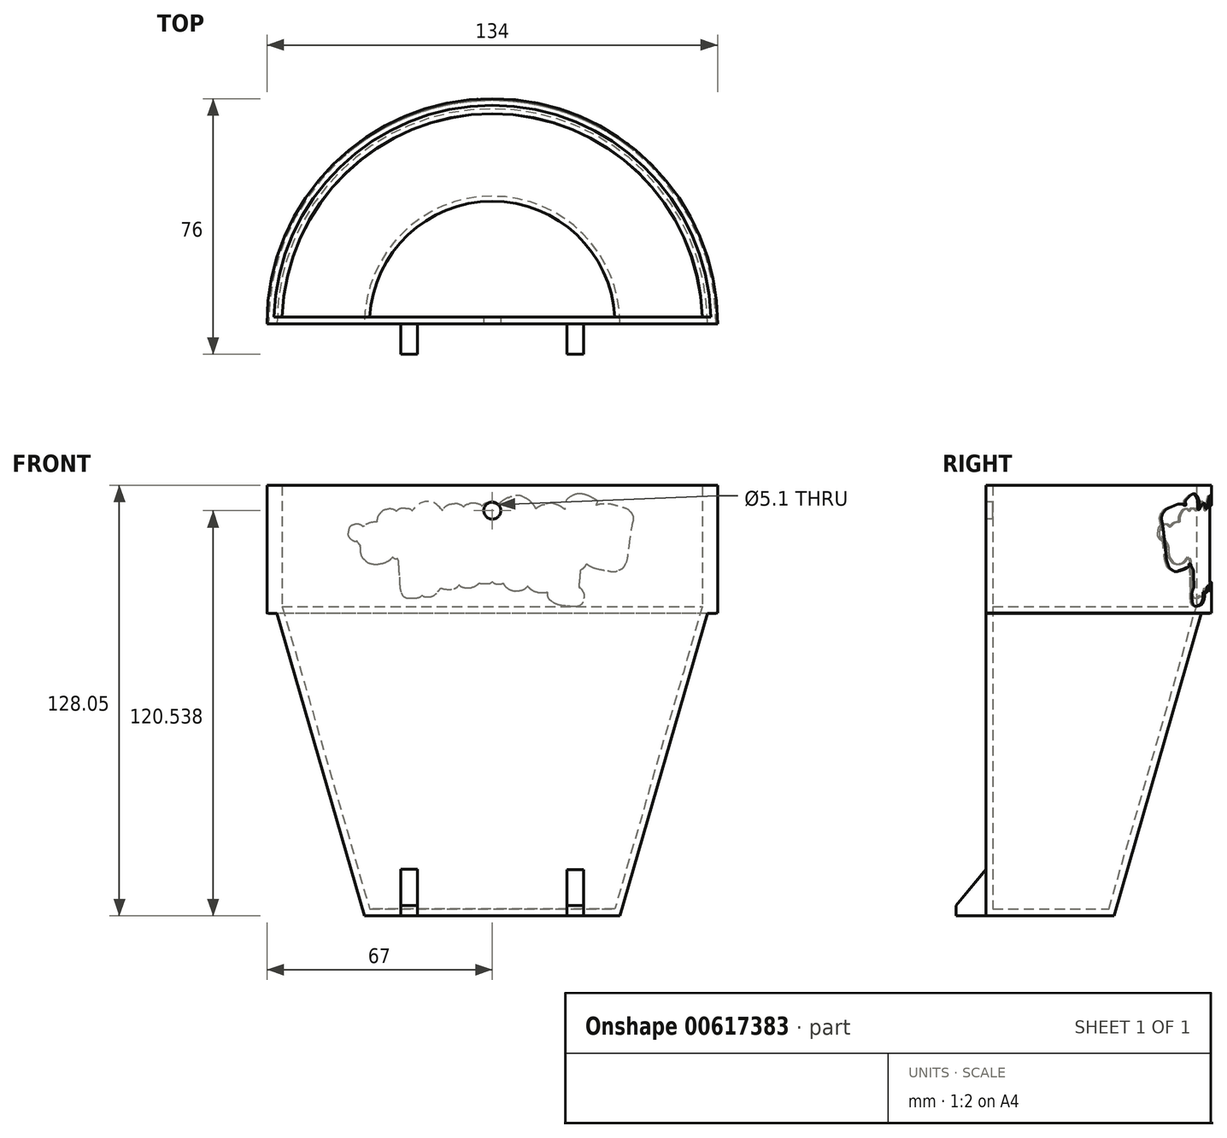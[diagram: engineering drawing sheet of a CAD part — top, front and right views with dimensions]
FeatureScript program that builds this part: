
annotation { "Feature Type Name" : "Feature", "Feature Type Description" : "" }
export const myFeature = defineFeature(function(context is Context, id is Id, definition is map)
    precondition{}
    {
        {
            var Q0;
            Q0=qCreatedBy(makeId("Front.planeOp"),FACE);
            var sketch = newSketch(context, id + "F0", { "sketchPlane" : qUnion([Q0])});
            skLineSegment(sketch, "E0", {"start": v(0, 56.42) * mm, "end": v(-67, 56.42) * mm});
            skLineSegment(sketch, "E1", {"start": v(-67, 56.42) * mm, "end": v(-67, 18.42) * mm});
            skLineSegment(sketch, "E2", {"start": v(0, -71.58) * mm, "end": v(-38, -71.58) * mm});
            skLineSegment(sketch, "E3", {"start": v(-67, 18.42) * mm, "end": v(-64, 18.42) * mm});
            skLineSegment(sketch, "E4", {"start": v(0, 56.42) * mm, "end": v(0, -71.58) * mm});
            skLineSegment(sketch, "E5", {"start": v(-64, 18.42) * mm, "end": v(-38, -71.58) * mm});
            skLineSegment(sketch, "E6.MirrorCS", {"start": v(0, 56.42) * mm, "end": v(67, 56.42) * mm});
            skLineSegment(sketch, "E7.MirrorCS", {"start": v(67, 56.42) * mm, "end": v(67, 18.42) * mm});
            skLineSegment(sketch, "E8.MirrorCS", {"start": v(67, 18.42) * mm, "end": v(64, 18.42) * mm});
            skLineSegment(sketch, "E9.MirrorCS", {"start": v(64, 18.42) * mm, "end": v(38, -71.58) * mm});
            skLineSegment(sketch, "E10.MirrorCS", {"start": v(0, -71.58) * mm, "end": v(38, -71.58) * mm});
            skSolve(sketch);
        }
        {
            var Q0;
            {var subQ0=sQuery(id+"F0.wireOp",EDGE,"E3");Q0=makeQuery(id+"F0.imprint","IMPRINT",FACE,{"disambiguationData":[TD([[makeQuery(id+"F0.imprint","IMPRINT",EDGE,{"derivedFrom":subQ0}),1.0]])]});}
            var Q1;
            {var subQ1=sQuery(id+"F0.wireOp",EDGE,"E0");Q1=makeQuery(id+"F0.imprint","IMPRINT",FACE,{"disambiguationData":[TD([[makeQuery(id+"F0.imprint","IMPRINT",EDGE,{"derivedFrom":subQ1}),1.0]])]});}
            var Q2;
            Q2=makeQuery(id+"F0.imprint","IMPRINT",FACE,{"disambiguationData":[TD([[makeQuery(id+"F0.imprint","IMPRINT",EDGE,{"derivedFrom":sQuery(id+"F0.wireOp",EDGE,"Kfnrekvc-ZjTY-c2iQ-cK4z-hKnBe4uEAVNk")}),1.0]])]});
            var Q3;
            Q3=sQuery(id+"F0.wireOp",EDGE,"E4");
            revolve(context, id + "F1", {"entities" : qUnion([Q0, Q1, Q2]), "axis" : qUnion([Q3]), "revolveType" : RevolveType.ONE_DIRECTION, "angle" : 180 * degree});
        }
        {
            var Q0;
            Q0=makeQuery(id+"FK2OT3XlAi37Aaq_1.splitOp","SPLIT",FACE,{"derivedFrom":makeQuery(id+"F1.opRevolve","SWEPT_FACE",FACE,{"disambiguationData":[OSD([sQuery(id+"F0.wireOp",EDGE,"E0")])]}),"isFromBackBody":true});
            shell(context, id + "F2", {"entities" : qUnion([Q0]), "thickness" : 2 * mm});
        }
        {
            var Q0;
            Q0=qCreatedBy(makeId("Front.planeOp"),FACE);
            var sketch = newSketch(context, id + "F3", { "sketchPlane" : qUnion([Q0])});
            skPoint(sketch, "E11.middle", {"position": v(0, -64.08) * mm});
            skLineSegment(sketch, "E12.bottom", {"start": v(-27.21, -56.57) * mm, "end": v(-22.21, -56.57) * mm});
            skLineSegment(sketch, "E12.top", {"start": v(-27.21, -71.57) * mm, "end": v(-22.21, -71.57) * mm});
            skLineSegment(sketch, "E12.left", {"start": v(-27.21, -56.57) * mm, "end": v(-27.21, -71.57) * mm});
            skLineSegment(sketch, "E12.right", {"start": v(-22.21, -56.57) * mm, "end": v(-22.21, -71.57) * mm});
            skPoint(sketch, "E12.middle", {"position": v(-24.71, -64.07) * mm});
            skLineSegment(sketch, "E13.bottom", {"start": v(22.21, -56.63) * mm, "end": v(27.21, -56.63) * mm});
            skLineSegment(sketch, "E13.top", {"start": v(22.21, -71.63) * mm, "end": v(27.21, -71.63) * mm});
            skLineSegment(sketch, "E13.left", {"start": v(22.21, -56.63) * mm, "end": v(22.21, -71.63) * mm});
            skLineSegment(sketch, "E13.right", {"start": v(27.21, -56.63) * mm, "end": v(27.21, -71.63) * mm});
            skPoint(sketch, "E13.middle", {"position": v(24.71, -64.13) * mm});
            skLineSegment(sketch, "E14", {"start": v(0, -71.68) * mm, "end": v(-22.21, -71.57) * mm, "construction": true});
            skLineSegment(sketch, "E15", {"start": v(0, -71.68) * mm, "end": v(22.21, -71.63) * mm, "construction": true});
            skSolve(sketch);
        }
        {
            var Q0;
            Q0=qSketchRegion(id+"F3",true);
            extrude(context, id + "F4", {"entities" : qUnion([Q0]), "operationType" : NewBodyOperationType.ADD, "depth" : 9 * mm});
        }
        {
            var Q0;
            Q0=qCreatedBy(makeId("Front.planeOp"),FACE);
            var sketch = newSketch(context, id + "F5", { "sketchPlane" : qUnion([Q0])});
            skCircle(sketch, "E16", {"center": v(0, 48.9) * mm, "radius": 2.55 * mm});
            skLineSegment(sketch, "E17", {"start": v(0, 56.46) * mm, "end": v(0, 51.46) * mm, "construction": true});
            skSolve(sketch);
        }
        {
            var Q0;
            {var subQ0=sQuery(id+"F5.wireOp",EDGE,"E16");var subQ1=sQuery(id+"F5.wireOp",EDGE,"mXHq6PA0-CqQh-Lv1D-GdnR-uttjTBgCqYAd");var subQ2=makeQuery(id+"F5.imprint","INTERSECT",VERTEX,{"disambiguationData":[OD(0.0)],"derivedFrom":[subQ1,subQ0]});Q0=makeQuery(id+"F5.imprint","IMPRINT",FACE,{"disambiguationData":[TD([[makeQuery(id+"F5.imprint","IMPRINT",EDGE,{"disambiguationData":[TD([[subQ2,1.0]])],"derivedFrom":subQ1}),1.0]])]});}
            var Q1;
            {var subQ0=sQuery(id+"F5.wireOp",EDGE,"E16");var subQ1=sQuery(id+"F5.wireOp",EDGE,"mXHq6PA0-CqQh-Lv1D-GdnR-uttjTBgCqYAd");var subQ2=makeQuery(id+"F5.imprint","INTERSECT",VERTEX,{"disambiguationData":[OD(0.0)],"derivedFrom":[subQ1,subQ0]});Q1=makeQuery(id+"F5.imprint","IMPRINT",FACE,{"disambiguationData":[TD([[makeQuery(id+"F5.imprint","IMPRINT",EDGE,{"disambiguationData":[TD([[subQ2,-1.0]])],"derivedFrom":subQ1}),-1.0]])]});}
            var Q2;
            {var subQ0=sQuery(id+"F5.wireOp",EDGE,"E16");var subQ1=sQuery(id+"F5.wireOp",EDGE,"mXHq6PA0-CqQh-Lv1D-GdnR-uttjTBgCqYAd");var subQ2=makeQuery(id+"F5.imprint","INTERSECT",VERTEX,{"disambiguationData":[OD(0.0)],"derivedFrom":[subQ1,subQ0]});Q2=makeQuery(id+"F5.imprint","IMPRINT",FACE,{"disambiguationData":[TD([[makeQuery(id+"F5.imprint","IMPRINT",EDGE,{"disambiguationData":[TD([[subQ2,-1.0]])],"derivedFrom":subQ1}),1.0]])]});}
            var Q3;
            Q3=makeQuery(id+"F5.imprint","IMPRINT",FACE,{"disambiguationData":[TD([[makeQuery(id+"F5.imprint","IMPRINT",EDGE,{"derivedFrom":sQuery(id+"F5.wireOp",EDGE,"3L3EtL6l-Z5xn-OpCV-56nK-jdjtkjkFmQCH")}),1.0]])]});
            var Q4;
            {var subQ0=sQuery(id+"F5.wireOp",EDGE,"E16");var subQ1=makeQuery(id+"F5.imprint","INTERSECT",VERTEX,{"derivedFrom":[subQ0,sQuery(id+"F5.wireOp",EDGE,"FsL0R7OM-7ciT-IbGp-vdo3-nhAMjBVExGBG")]});Q4=makeQuery(id+"F5.imprint","IMPRINT",FACE,{"disambiguationData":[TD([[makeQuery(id+"F5.imprint","IMPRINT",EDGE,{"disambiguationData":[TD([[subQ1,1.0]])],"derivedFrom":subQ0}),1.0]])]});}
            var Q5;
            Q5=sQuery(id+"F5.wireOp",EDGE,"mXHq6PA0-CqQh-Lv1D-GdnR-uttjTBgCqYAd");
            var Q6;
            Q6=sQuery(id+"F5.wireOp",EDGE,"E16");
            extrude(context, id + "F6", {"entities" : qUnion([Q0, Q1, Q2, Q3, Q4]), "operationType" : NewBodyOperationType.REMOVE, "surfaceEntities" : qUnion([Q5, Q6]), "oppositeDirection" : true, "depth" : 10 * mm, "offsetDistance" : 25 * mm});
        }
        {
            var Q0;
            Q0=makeQuery(id+"F4.opExtrude","CAP_EDGE",EDGE,{"disambiguationData":[OSD([sQuery(id+"F3.wireOp",EDGE,"E11.bottom")])],"isStart":false});
            var Q1;
            Q1=makeQuery(id+"F4.opExtrude","CAP_EDGE",EDGE,{"disambiguationData":[OSD([sQuery(id+"F3.wireOp",EDGE,"E12.bottom")])],"isStart":false});
            var Q2;
            Q2=makeQuery(id+"F4.opExtrude","CAP_EDGE",EDGE,{"disambiguationData":[OSD([sQuery(id+"F3.wireOp",EDGE,"E13.bottom")])],"isStart":false});
            chamfer(context, id + "F7", {"entities" : qUnion([Q0, Q1, Q2]), "chamferType" : ChamferType.OFFSET_ANGLE, "width" : 10 * mm, "oppositeDirection" : false, "angle" : 50 * degree, "tangentPropagation" : true});
        }
        {
            var Q0;
            Q0=makeQuery(id+"F2.opShell","OFFSET_FACE",FACE,{"disambiguationData":[OSD([sQuery(id+"F0.wireOp",EDGE,"E0"),sQuery(id+"F0.wireOp",EDGE,"E1"),sQuery(id+"F0.wireOp",EDGE,"E2"),sQuery(id+"F0.wireOp",EDGE,"E3"),sQuery(id+"F0.wireOp",EDGE,"E4"),sQuery(id+"F0.wireOp",EDGE,"E5")])]});
            cPlane(context, id + "F8", {"entities" : qUnion([Q0]), "cplaneType" : CPlaneType.OFFSET, "offset" : 66.8 * mm, "width" : 150 * mm, "height" : 150 * mm});
        }
        {
            var Q0;
            Q0=makeQuery(id+"F1.opRevolve","SWEPT_FACE",FACE,{"disambiguationData":[OSD([sQuery(id+"F0.wireOp",EDGE,"E0")])]});
            var sketch = newSketch(context, id + "F9", { "sketchPlane" : qUnion([Q0])});
            skCircle(sketch, "E18", {"center": v(0, 0) * mm, "radius": 67.75 * mm});
            skCircle(sketch, "E19", {"center": v(0, 0) * mm, "radius": 91 * mm});
            skSolve(sketch);
        }
        {
            var Q0;
            Q0=qSketchRegion(id+"F9",true);
            extrude(context, id + "F10", {"entities" : qUnion([Q0]), "operationType" : NewBodyOperationType.REMOVE, "oppositeDirection" : true, "depth" : 124 * mm});
        }
        {
            var Q0;
            Q0=qCreatedBy(id+"F8.planeOp",FACE);
            var sketch = newSketch(context, id + "F11", { "sketchPlane" : qUnion([Q0])});
            skFitSpline(sketch, "E20", {"points": [v(-14.21, 60.71) * mm, v(-15.23, 60.8) * mm, v(-17.15, 61.07) * mm, v(-17.98, 61.24) * mm]});
            skFitSpline(sketch, "E21", {"points": [v(-17.98, 61.24) * mm, v(-19.27, 61.5) * mm, v(-20.2, 61.84) * mm, v(-21.41, 62.47) * mm]});
            skFitSpline(sketch, "E22", {"points": [v(-21.41, 62.47) * mm, v(-24.2, 63.93) * mm, v(-26.13, 64.66) * mm, v(-28.48, 65.15) * mm]});
            skFitSpline(sketch, "E23", {"points": [v(-28.48, 65.15) * mm, v(-29.29, 65.32) * mm, v(-30, 65.37) * mm, v(-32.2, 65.43) * mm]});
            skFitSpline(sketch, "E24", {"points": [v(-32.2, 65.43) * mm, v(-35.22, 65.52) * mm, v(-35.76, 65.6) * mm, v(-36.93, 66.16) * mm]});
            skFitSpline(sketch, "E25", {"points": [v(-36.93, 66.16) * mm, v(-38.77, 67.04) * mm, v(-39.83, 68.44) * mm, v(-40.02, 70.25) * mm]});
            skFitSpline(sketch, "E26", {"points": [v(-40.02, 70.25) * mm, v(-40.16, 71.57) * mm, v(-40.28, 76.7) * mm, v(-40.26, 80.14) * mm]});
            skFitSpline(sketch, "E27", {"points": [v(-39.96, 84.14) * mm, v(-39.6, 85.02) * mm, v(-39.23, 85.55) * mm, v(-38.6, 86.04) * mm]});
            skFitSpline(sketch, "E28", {"points": [v(-38.6, 86.04) * mm, v(-37.32, 87.06) * mm, v(-35.24, 87.34) * mm, v(-32.5, 86.87) * mm]});
            skFitSpline(sketch, "E29", {"points": [v(-32.5, 86.87) * mm, v(-31.47, 86.7) * mm, v(-30.34, 86.4) * mm, v(-28.67, 85.86) * mm]});
            skFitSpline(sketch, "E30", {"points": [v(-28.67, 85.86) * mm, v(-26.48, 85.16) * mm, v(-25.24, 84.96) * mm, v(-23.15, 84.96) * mm]});
            skFitSpline(sketch, "E31", {"points": [v(-23.15, 84.96) * mm, v(-22.35, 84.96) * mm, v(-21.18, 85.03) * mm, v(-20.54, 85.12) * mm]});
            skFitSpline(sketch, "E32", {"points": [v(-20.54, 85.12) * mm, v(-18.34, 85.42) * mm, v(-15.77, 86.13) * mm, v(-14.88, 86.67) * mm]});
            skFitSpline(sketch, "E33", {"points": [v(-14.88, 86.67) * mm, v(-14.07, 87.17) * mm, v(-12.87, 87.67) * mm, v(-11.9, 87.91) * mm]});
            skFitSpline(sketch, "E34", {"points": [v(-11.9, 87.91) * mm, v(-11.18, 88.1) * mm, v(-10.77, 88.13) * mm, v(-9.58, 88.13) * mm]});
            skFitSpline(sketch, "E35", {"points": [v(-9.58, 88.13) * mm, v(-7.91, 88.13) * mm, v(-7.18, 87.99) * mm, v(-5.29, 87.27) * mm]});
            skFitSpline(sketch, "E36", {"points": [v(-5.29, 87.27) * mm, v(-3.99, 86.78) * mm, v(-2.9, 86.45) * mm, v(-1.6, 86.14) * mm]});
            skFitSpline(sketch, "E37", {"points": [v(-1.6, 86.14) * mm, v(-1.1, 86.03) * mm, v(-0.13, 85.78) * mm, v(0.55, 85.59) * mm]});
            skFitSpline(sketch, "E38", {"points": [v(0.55, 85.59) * mm, v(2.03, 85.17) * mm, v(2.79, 85.14) * mm, v(4.3, 85.4) * mm]});
            skFitSpline(sketch, "E39", {"points": [v(4.3, 85.4) * mm, v(6.34, 85.76) * mm, v(7.65, 85.52) * mm, v(10.1, 84.34) * mm]});
            skFitSpline(sketch, "E40", {"points": [v(10.1, 84.34) * mm, v(12.42, 83.22) * mm, v(13.55, 82.94) * mm, v(14.56, 83.25) * mm]});
            skFitSpline(sketch, "E41", {"points": [v(14.56, 83.25) * mm, v(14.85, 83.34) * mm, v(15.6, 83.69) * mm, v(16.21, 84.03) * mm]});
            skFitSpline(sketch, "E42", {"points": [v(16.21, 84.03) * mm, v(16.83, 84.37) * mm, v(17.63, 84.77) * mm, v(17.97, 84.9) * mm]});
            skFitSpline(sketch, "E43", {"points": [v(17.97, 84.9) * mm, v(19, 85.32) * mm, v(21.27, 85.96) * mm, v(22.8, 85.75) * mm]});
            skFitSpline(sketch, "E44", {"points": [v(22.8, 85.75) * mm, v(25.09, 84.74) * mm, v(26.57, 84.16) * mm, v(27.89, 83.82) * mm]});
            skFitSpline(sketch, "E45", {"points": [v(27.89, 83.82) * mm, v(28.82, 83.6) * mm, v(29.1, 83.56) * mm, v(30.58, 83.57) * mm]});
            skFitSpline(sketch, "E46", {"points": [v(30.58, 83.57) * mm, v(32.1, 83.57) * mm, v(32.41, 83.6) * mm, v(34.6, 84) * mm]});
            skFitSpline(sketch, "E47", {"points": [v(34.6, 84) * mm, v(36.58, 84.35) * mm, v(37.14, 84.42) * mm, v(38.19, 84.42) * mm]});
            skFitSpline(sketch, "E48", {"points": [v(38.19, 84.42) * mm, v(39.58, 84.42) * mm, v(39.98, 84.31) * mm, v(40.62, 83.8) * mm]});
            skFitSpline(sketch, "E49", {"points": [v(40.62, 83.8) * mm, v(41.14, 83.38) * mm, v(41.5, 82.8) * mm, v(41.88, 81.74) * mm]});
            skFitSpline(sketch, "E50", {"points": [v(41.88, 81.74) * mm, v(42.44, 80.2) * mm, v(42.49, 79.85) * mm, v(42.49, 77.2) * mm]});
            skFitSpline(sketch, "E51", {"points": [v(42.49, 77.2) * mm, v(42.48, 74.69) * mm, v(42.34, 72.96) * mm, v(41.92, 70.56) * mm]});
            skFitSpline(sketch, "E52", {"points": [v(41.92, 70.56) * mm, v(41.56, 68.48) * mm, v(41.46, 68.19) * mm, v(40.86, 67.68) * mm]});
            skFitSpline(sketch, "E53", {"points": [v(40.86, 67.68) * mm, v(40.27, 67.18) * mm, v(39.77, 67.05) * mm, v(38.23, 67.05) * mm]});
            skFitSpline(sketch, "E54", {"points": [v(38.23, 67.05) * mm, v(35.56, 67.04) * mm, v(34.05, 67.16) * mm, v(33.1, 67.44) * mm]});
            skFitSpline(sketch, "E55", {"points": [v(33.1, 67.44) * mm, v(31.4, 67.95) * mm, v(30.14, 67.86) * mm, v(28.22, 67.1) * mm]});
            skFitSpline(sketch, "E56", {"points": [v(28.22, 67.1) * mm, v(26.75, 66.51) * mm, v(26.28, 66.21) * mm, v(25.37, 65.28) * mm]});
            skFitSpline(sketch, "E57", {"points": [v(25.37, 65.28) * mm, v(23.19, 63.06) * mm, v(21.33, 61.94) * mm, v(19.52, 61.74) * mm]});
            skFitSpline(sketch, "E58", {"points": [v(19.52, 61.74) * mm, v(18.5, 61.63) * mm, v(17.41, 61.74) * mm, v(15.77, 62.11) * mm]});
            skFitSpline(sketch, "E59", {"points": [v(15.77, 62.11) * mm, v(13.66, 62.6) * mm, v(12.37, 62.66) * mm, v(8.71, 62.47) * mm]});
            skFitSpline(sketch, "E60", {"points": [v(8.71, 62.47) * mm, v(6.82, 62.37) * mm, v(4.44, 62.32) * mm, v(2.66, 62.33) * mm]});
            skFitSpline(sketch, "E61", {"points": [v(2.66, 62.33) * mm, v(0.28, 62.35) * mm, v(-0.53, 62.32) * mm, v(-1.6, 62.18) * mm]});
            skFitSpline(sketch, "E62", {"points": [v(-1.6, 62.18) * mm, v(-3.69, 61.9) * mm, v(-5.8, 61.56) * mm, v(-8.26, 61.08) * mm]});
            skFitSpline(sketch, "E63", {"points": [v(-8.26, 61.08) * mm, v(-10.46, 60.66) * mm, v(-10.6, 60.65) * mm, v(-12.2, 60.67) * mm]});
            skFitSpline(sketch, "E64", {"points": [v(-12.2, 60.67) * mm, v(-13.1, 60.68) * mm, v(-14, 60.7) * mm, v(-14.21, 60.71) * mm]});
            skLineSegment(sketch, "E65", {"start": v(-40.26, 80.14) * mm, "end": v(-40.23, 83.46) * mm});
            skLineSegment(sketch, "E66", {"start": v(-40.23, 83.46) * mm, "end": v(-39.96, 84.14) * mm});
            skLineSegment(sketch, "E67", {"start": v(-39.96, 84.14) * mm, "end": v(-40.26, 80.14) * mm});
            skFitSpline(sketch, "E68", {"points": [v(-114.19, 54.15) * mm, v(-115.23, 54.24) * mm, v(-117.2, 54.5) * mm, v(-118.04, 54.68) * mm]});
            skFitSpline(sketch, "E69", {"points": [v(-118.04, 54.68) * mm, v(-119.36, 54.94) * mm, v(-120.32, 55.28) * mm, v(-121.56, 55.91) * mm]});
            skFitSpline(sketch, "E70", {"points": [v(-121.56, 55.91) * mm, v(-124.41, 57.37) * mm, v(-126.39, 58.1) * mm, v(-128.8, 58.6) * mm]});
            skFitSpline(sketch, "E71", {"points": [v(-128.8, 58.6) * mm, v(-129.62, 58.76) * mm, v(-130.36, 58.81) * mm, v(-132.61, 58.87) * mm]});
            skFitSpline(sketch, "E72", {"points": [v(-132.61, 58.87) * mm, v(-135.7, 58.96) * mm, v(-136.25, 59.04) * mm, v(-137.45, 59.6) * mm]});
            skFitSpline(sketch, "E73", {"points": [v(-137.45, 59.6) * mm, v(-139.33, 60.48) * mm, v(-140.42, 61.88) * mm, v(-140.62, 63.69) * mm]});
            skFitSpline(sketch, "E74", {"points": [v(-140.62, 63.69) * mm, v(-140.76, 65) * mm, v(-140.89, 70.13) * mm, v(-140.86, 73.57) * mm]});
            skFitSpline(sketch, "E75", {"points": [v(-140.55, 77.57) * mm, v(-140.19, 78.46) * mm, v(-139.8, 78.98) * mm, v(-139.17, 79.47) * mm]});
            skFitSpline(sketch, "E76", {"points": [v(-139.17, 79.47) * mm, v(-137.85, 80.5) * mm, v(-135.72, 80.77) * mm, v(-132.9, 80.3) * mm]});
            skFitSpline(sketch, "E77", {"points": [v(-132.9, 80.3) * mm, v(-131.86, 80.13) * mm, v(-130.7, 79.83) * mm, v(-129, 79.3) * mm]});
            skFitSpline(sketch, "E78", {"points": [v(-129, 79.3) * mm, v(-126.75, 78.6) * mm, v(-125.48, 78.4) * mm, v(-123.34, 78.4) * mm]});
            skFitSpline(sketch, "E79", {"points": [v(-123.34, 78.4) * mm, v(-122.51, 78.4) * mm, v(-121.32, 78.47) * mm, v(-120.66, 78.56) * mm]});
            skFitSpline(sketch, "E80", {"points": [v(-120.66, 78.56) * mm, v(-118.41, 78.86) * mm, v(-115.78, 79.56) * mm, v(-114.86, 80.1) * mm]});
            skFitSpline(sketch, "E81", {"points": [v(-114.86, 80.1) * mm, v(-114.04, 80.6) * mm, v(-112.8, 81.1) * mm, v(-111.81, 81.35) * mm]});
            skFitSpline(sketch, "E82", {"points": [v(-111.81, 81.35) * mm, v(-111.08, 81.53) * mm, v(-110.66, 81.57) * mm, v(-109.44, 81.57) * mm]});
            skFitSpline(sketch, "E83", {"points": [v(-109.44, 81.57) * mm, v(-107.73, 81.57) * mm, v(-106.98, 81.42) * mm, v(-105.04, 80.7) * mm]});
            skFitSpline(sketch, "E84", {"points": [v(-105.04, 80.7) * mm, v(-103.71, 80.21) * mm, v(-102.6, 79.88) * mm, v(-101.27, 79.58) * mm]});
            skFitSpline(sketch, "E85", {"points": [v(-101.27, 79.58) * mm, v(-100.75, 79.46) * mm, v(-99.76, 79.21) * mm, v(-99.06, 79.02) * mm]});
            skFitSpline(sketch, "E86", {"points": [v(-99.06, 79.02) * mm, v(-97.55, 78.61) * mm, v(-96.78, 78.57) * mm, v(-95.22, 78.84) * mm]});
            skFitSpline(sketch, "E87", {"points": [v(-95.22, 78.84) * mm, v(-93.14, 79.2) * mm, v(-91.8, 78.96) * mm, v(-89.3, 77.78) * mm]});
            skFitSpline(sketch, "E88", {"points": [v(-89.3, 77.78) * mm, v(-86.91, 76.66) * mm, v(-85.75, 76.38) * mm, v(-84.72, 76.69) * mm]});
            skFitSpline(sketch, "E89", {"points": [v(-84.72, 76.69) * mm, v(-84.42, 76.77) * mm, v(-83.66, 77.12) * mm, v(-83.03, 77.47) * mm]});
            skFitSpline(sketch, "E90", {"points": [v(-83.03, 77.47) * mm, v(-82.39, 77.8) * mm, v(-81.58, 78.2) * mm, v(-81.22, 78.34) * mm]});
            skFitSpline(sketch, "E91", {"points": [v(-81.22, 78.34) * mm, v(-80.17, 78.76) * mm, v(-77.85, 79.4) * mm, v(-76.27, 79.19) * mm]});
            skFitSpline(sketch, "E92", {"points": [v(-76.27, 79.19) * mm, v(-73.94, 78.17) * mm, v(-72.42, 77.6) * mm, v(-71.07, 77.26) * mm]});
            skFitSpline(sketch, "E93", {"points": [v(-71.07, 77.26) * mm, v(-70.12, 77.03) * mm, v(-69.83, 77) * mm, v(-68.31, 77) * mm]});
            skFitSpline(sketch, "E94", {"points": [v(-68.31, 77) * mm, v(-66.75, 77) * mm, v(-66.43, 77.04) * mm, v(-64.2, 77.43) * mm]});
            skFitSpline(sketch, "E95", {"points": [v(-64.2, 77.43) * mm, v(-62.16, 77.79) * mm, v(-61.6, 77.85) * mm, v(-60.52, 77.85) * mm]});
            skFitSpline(sketch, "E96", {"points": [v(-60.52, 77.85) * mm, v(-59.1, 77.85) * mm, v(-58.69, 77.75) * mm, v(-58.03, 77.23) * mm]});
            skFitSpline(sketch, "E97", {"points": [v(-58.03, 77.23) * mm, v(-57.5, 76.81) * mm, v(-57.13, 76.23) * mm, v(-56.74, 75.17) * mm]});
            skFitSpline(sketch, "E98", {"points": [v(-56.74, 75.17) * mm, v(-56.16, 73.64) * mm, v(-56.11, 73.29) * mm, v(-56.12, 70.64) * mm]});
            skFitSpline(sketch, "E99", {"points": [v(-56.12, 70.64) * mm, v(-56.12, 68.12) * mm, v(-56.27, 66.4) * mm, v(-56.7, 64) * mm]});
            skFitSpline(sketch, "E100", {"points": [v(-56.7, 64) * mm, v(-57.06, 61.92) * mm, v(-57.17, 61.63) * mm, v(-57.78, 61.12) * mm]});
            skFitSpline(sketch, "E101", {"points": [v(-57.78, 61.12) * mm, v(-58.38, 60.61) * mm, v(-58.9, 60.5) * mm, v(-60.48, 60.49) * mm]});
            skFitSpline(sketch, "E102", {"points": [v(-60.48, 60.49) * mm, v(-63.2, 60.48) * mm, v(-64.75, 60.6) * mm, v(-65.73, 60.88) * mm]});
            skFitSpline(sketch, "E103", {"points": [v(-65.73, 60.88) * mm, v(-67.47, 61.39) * mm, v(-68.76, 61.3) * mm, v(-70.73, 60.53) * mm]});
            skFitSpline(sketch, "E104", {"points": [v(-70.73, 60.53) * mm, v(-72.23, 59.95) * mm, v(-72.71, 59.65) * mm, v(-73.65, 58.72) * mm]});
            skFitSpline(sketch, "E105", {"points": [v(-73.65, 58.72) * mm, v(-75.88, 56.5) * mm, v(-77.78, 55.38) * mm, v(-79.64, 55.18) * mm]});
            skFitSpline(sketch, "E106", {"points": [v(-79.64, 55.18) * mm, v(-80.69, 55.07) * mm, v(-81.8, 55.18) * mm, v(-83.48, 55.55) * mm]});
            skFitSpline(sketch, "E107", {"points": [v(-83.48, 55.55) * mm, v(-85.64, 56.03) * mm, v(-86.96, 56.1) * mm, v(-90.7, 55.9) * mm]});
            skFitSpline(sketch, "E108", {"points": [v(-90.7, 55.9) * mm, v(-92.64, 55.8) * mm, v(-95.08, 55.75) * mm, v(-96.9, 55.77) * mm]});
            skFitSpline(sketch, "E109", {"points": [v(-96.9, 55.77) * mm, v(-99.34, 55.79) * mm, v(-100.17, 55.76) * mm, v(-101.27, 55.62) * mm]});
            skFitSpline(sketch, "E110", {"points": [v(-101.27, 55.62) * mm, v(-103.4, 55.34) * mm, v(-105.57, 55) * mm, v(-108.1, 54.52) * mm]});
            skFitSpline(sketch, "E111", {"points": [v(-108.1, 54.52) * mm, v(-110.34, 54.1) * mm, v(-110.48, 54.09) * mm, v(-112.12, 54.1) * mm]});
            skFitSpline(sketch, "E112", {"points": [v(-112.12, 54.1) * mm, v(-113.05, 54.11) * mm, v(-113.98, 54.14) * mm, v(-114.19, 54.15) * mm]});
            skLineSegment(sketch, "E113", {"start": v(-140.86, 73.57) * mm, "end": v(-140.83, 76.9) * mm});
            skLineSegment(sketch, "E114", {"start": v(-140.83, 76.9) * mm, "end": v(-140.55, 77.57) * mm});
            skLineSegment(sketch, "E115", {"start": v(-140.55, 77.57) * mm, "end": v(-140.86, 73.57) * mm});
            skLineSegment(sketch, "E116", {"start": v(-26.02, 25.94) * mm, "end": v(-25.8, 26.08) * mm});
            skLineSegment(sketch, "E117", {"start": v(-25.8, 26.08) * mm, "end": v(-25.83, 26.31) * mm});
            skLineSegment(sketch, "E118", {"start": v(-1.78, 50.63) * mm, "end": v(-1.69, 50.5) * mm});
            skLineSegment(sketch, "E119", {"start": v(-1.69, 50.5) * mm, "end": v(-1.46, 50.6) * mm});
            skLineSegment(sketch, "E120", {"start": v(2.84, 50.53) * mm, "end": v(3.08, 50.36) * mm});
            skLineSegment(sketch, "E121", {"start": v(3.08, 50.36) * mm, "end": v(3.3, 50.49) * mm});
            skLineSegment(sketch, "E122", {"start": v(8.3, 50.26) * mm, "end": v(8.5, 50.11) * mm});
            skLineSegment(sketch, "E123", {"start": v(8.5, 50.11) * mm, "end": v(8.96, 50.34) * mm});
            skLineSegment(sketch, "E124", {"start": v(14.7, 49.22) * mm, "end": v(14.89, 49) * mm});
            skLineSegment(sketch, "E125", {"start": v(14.89, 49) * mm, "end": v(15.19, 49.27) * mm});
            skLineSegment(sketch, "E126", {"start": v(23.53, 49.23) * mm, "end": v(23.82, 48.93) * mm});
            skLineSegment(sketch, "E127", {"start": v(23.82, 48.93) * mm, "end": v(23.94, 49) * mm});
            skLineSegment(sketch, "E128", {"start": v(28.19, 49.04) * mm, "end": v(28.51, 48.86) * mm});
            skLineSegment(sketch, "E129", {"start": v(28.51, 48.86) * mm, "end": v(28.8, 48.98) * mm});
            skLineSegment(sketch, "E130", {"start": v(40.37, 39.78) * mm, "end": v(40.13, 39.78) * mm});
            skLineSegment(sketch, "E131", {"start": v(40.13, 39.78) * mm, "end": v(39.94, 39.4) * mm});
            skLineSegment(sketch, "E132", {"start": v(39.48, 38.75) * mm, "end": v(39.2, 38.47) * mm});
            skLineSegment(sketch, "E133", {"start": v(39.2, 38.47) * mm, "end": v(39.25, 38.2) * mm});
            skLineSegment(sketch, "E134", {"start": v(29.94, 34.67) * mm, "end": v(29.63, 34.97) * mm});
            skLineSegment(sketch, "E135", {"start": v(29.63, 34.97) * mm, "end": v(29.38, 34.84) * mm});
            skLineSegment(sketch, "E136", {"start": v(28.4, 34.58) * mm, "end": v(28.05, 34.55) * mm});
            skLineSegment(sketch, "E137", {"start": v(28.05, 34.55) * mm, "end": v(28, 34.08) * mm});
            skLineSegment(sketch, "E138", {"start": v(21.17, 23.42) * mm, "end": v(20.91, 23.57) * mm});
            skLineSegment(sketch, "E139", {"start": v(20.91, 23.57) * mm, "end": v(20.59, 23.46) * mm});
            skLineSegment(sketch, "E140", {"start": v(10.19, 26.42) * mm, "end": v(9.86, 26.74) * mm});
            skLineSegment(sketch, "E141", {"start": v(9.86, 26.74) * mm, "end": v(9.7, 26.63) * mm});
            skLineSegment(sketch, "E142", {"start": v(0.27, 27.5) * mm, "end": v(-0.02, 27.65) * mm});
            skLineSegment(sketch, "E143", {"start": v(-0.02, 27.65) * mm, "end": v(-0.2, 27.55) * mm});
            skLineSegment(sketch, "E144", {"start": v(-10.21, 26.14) * mm, "end": v(-10.5, 26.42) * mm});
            skLineSegment(sketch, "E145", {"start": v(-10.5, 26.42) * mm, "end": v(-10.7, 26.2) * mm});
            skLineSegment(sketch, "E146", {"start": v(-24.47, 20.52) * mm, "end": v(-24.47, 20.52) * mm});
            skFitSpline(sketch, "E147", {"points": [v(-24.47, 20.52) * mm, v(-25.87, 20.68) * mm, v(-26.93, 21.53) * mm, v(-27.26, 22.75) * mm]});
            skFitSpline(sketch, "E148", {"points": [v(-27.26, 22.75) * mm, v(-27.43, 23.4) * mm, v(-27.33, 24.23) * mm, v(-26.99, 24.87) * mm]});
            skFitSpline(sketch, "E149", {"points": [v(-26.99, 24.87) * mm, v(-26.8, 25.22) * mm, v(-26.34, 25.73) * mm, v(-26.02, 25.94) * mm]});
            skFitSpline(sketch, "E150", {"points": [v(-25.83, 26.31) * mm, v(-25.85, 26.45) * mm, v(-25.9, 26.98) * mm, v(-25.96, 27.5) * mm]});
            skFitSpline(sketch, "E151", {"points": [v(-25.96, 27.5) * mm, v(-26.02, 28.02) * mm, v(-26.1, 28.78) * mm, v(-26.12, 29.18) * mm]});
            skFitSpline(sketch, "E152", {"points": [v(-26.12, 29.18) * mm, v(-26.15, 29.78) * mm, v(-26.29, 30.94) * mm, v(-26.36, 31.28) * mm]});
            skFitSpline(sketch, "E153", {"points": [v(-26.36, 31.28) * mm, v(-26.37, 31.34) * mm, v(-26.48, 31.43) * mm, v(-26.66, 31.52) * mm]});
            skFitSpline(sketch, "E154", {"points": [v(-26.66, 31.52) * mm, v(-26.86, 31.62) * mm, v(-27.1, 31.8) * mm, v(-27.37, 32.08) * mm]});
            skFitSpline(sketch, "E155", {"points": [v(-27.37, 32.08) * mm, v(-27.6, 32.3) * mm, v(-27.8, 32.5) * mm, v(-27.8, 32.53) * mm]});
            skFitSpline(sketch, "E156", {"points": [v(-27.8, 32.53) * mm, v(-27.83, 32.6) * mm, v(-28.07, 33.03) * mm, v(-28.1, 33.03) * mm]});
            skFitSpline(sketch, "E157", {"points": [v(-28.1, 33.03) * mm, v(-28.11, 33.03) * mm, v(-28.23, 32.95) * mm, v(-28.36, 32.85) * mm]});
            skFitSpline(sketch, "E158", {"points": [v(-28.36, 32.85) * mm, v(-28.62, 32.66) * mm, v(-29.9, 32) * mm, v(-30.16, 31.93) * mm]});
            skFitSpline(sketch, "E159", {"points": [v(-30.16, 31.93) * mm, v(-30.17, 31.93) * mm, v(-30.3, 31.88) * mm, v(-30.46, 31.83) * mm]});
            skFitSpline(sketch, "E160", {"points": [v(-30.46, 31.83) * mm, v(-31.04, 31.64) * mm, v(-32.78, 31.26) * mm, v(-34.31, 31) * mm]});
            skFitSpline(sketch, "E161", {"points": [v(-34.31, 31) * mm, v(-35.8, 30.76) * mm, v(-36.68, 30.8) * mm, v(-37.6, 31.2) * mm]});
            skFitSpline(sketch, "E162", {"points": [v(-37.6, 31.2) * mm, v(-38.47, 31.56) * mm, v(-39.17, 32.22) * mm, v(-39.6, 33.06) * mm]});
            skFitSpline(sketch, "E163", {"points": [v(-39.6, 33.06) * mm, v(-40, 33.84) * mm, v(-40.35, 35.55) * mm, v(-40.72, 38.4) * mm]});
            skFitSpline(sketch, "E164", {"points": [v(-40.72, 38.4) * mm, v(-40.89, 39.7) * mm, v(-41.52, 43.94) * mm, v(-41.63, 44.49) * mm]});
            skFitSpline(sketch, "E165", {"points": [v(-41.63, 44.49) * mm, v(-41.67, 44.68) * mm, v(-41.76, 45.12) * mm, v(-41.85, 45.48) * mm]});
            skFitSpline(sketch, "E166", {"points": [v(-41.85, 45.48) * mm, v(-42.05, 46.33) * mm, v(-42.06, 46.82) * mm, v(-41.89, 47.33) * mm]});
            skFitSpline(sketch, "E167", {"points": [v(-41.89, 47.33) * mm, v(-41.73, 47.78) * mm, v(-41.54, 48.1) * mm, v(-41.2, 48.44) * mm]});
            skFitSpline(sketch, "E168", {"points": [v(-41.2, 48.44) * mm, v(-40.46, 49.18) * mm, v(-39.4, 49.67) * mm, v(-37.32, 50.25) * mm]});
            skFitSpline(sketch, "E169", {"points": [v(-37.32, 50.25) * mm, v(-35.54, 50.75) * mm, v(-34.54, 50.9) * mm, v(-33.22, 50.86) * mm]});
            skFitSpline(sketch, "E170", {"points": [v(-33.22, 50.86) * mm, v(-32.3, 50.84) * mm, v(-31.86, 50.78) * mm, v(-31.25, 50.57) * mm]});
            skFitSpline(sketch, "E171", {"points": [v(-31.25, 50.57) * mm, v(-31.1, 50.52) * mm, v(-30.97, 50.49) * mm, v(-30.96, 50.5) * mm]});
            skFitSpline(sketch, "E172", {"points": [v(-30.96, 50.5) * mm, v(-30.95, 50.5) * mm, v(-31.04, 50.77) * mm, v(-31.15, 51.09) * mm]});
            skFitSpline(sketch, "E173", {"points": [v(-31.15, 51.09) * mm, v(-31.27, 51.4) * mm, v(-31.37, 51.67) * mm, v(-31.37, 51.67) * mm]});
            skFitSpline(sketch, "E174", {"points": [v(-31.37, 51.67) * mm, v(-31.37, 51.72) * mm, v(-29.67, 52.78) * mm, v(-29.26, 52.99) * mm]});
            skFitSpline(sketch, "E175", {"points": [v(-29.26, 52.99) * mm, v(-28.64, 53.3) * mm, v(-27.39, 53.72) * mm, v(-26.8, 53.83) * mm]});
            skFitSpline(sketch, "E176", {"points": [v(-26.8, 53.83) * mm, v(-26.2, 53.93) * mm, v(-25.4, 53.91) * mm, v(-24.85, 53.78) * mm]});
            skFitSpline(sketch, "E177", {"points": [v(-24.85, 53.78) * mm, v(-24.66, 53.73) * mm, v(-24.07, 53.48) * mm, v(-23.82, 53.34) * mm]});
            skFitSpline(sketch, "E178", {"points": [v(-23.82, 53.34) * mm, v(-22.55, 52.6) * mm, v(-21.76, 51.33) * mm, v(-21.6, 49.73) * mm]});
            skFitSpline(sketch, "E179", {"points": [v(-21.6, 49.73) * mm, v(-21.58, 49.47) * mm, v(-21.55, 49.26) * mm, v(-21.55, 49.26) * mm]});
            skFitSpline(sketch, "E180", {"points": [v(-21.55, 49.26) * mm, v(-21.54, 49.25) * mm, v(-21.38, 49.37) * mm, v(-21.2, 49.53) * mm]});
            skFitSpline(sketch, "E181", {"points": [v(-21.2, 49.53) * mm, v(-20.79, 49.86) * mm, v(-20.28, 50.17) * mm, v(-19.76, 50.41) * mm]});
            skFitSpline(sketch, "E182", {"points": [v(-19.76, 50.41) * mm, v(-19.56, 50.51) * mm, v(-19.38, 50.6) * mm, v(-19.37, 50.6) * mm]});
            skFitSpline(sketch, "E183", {"points": [v(-19.37, 50.6) * mm, v(-19.35, 50.6) * mm, v(-19.16, 50.66) * mm, v(-18.93, 50.74) * mm]});
            skFitSpline(sketch, "E184", {"points": [v(-18.93, 50.74) * mm, v(-17.9, 51.08) * mm, v(-16.84, 51.1) * mm, v(-15.66, 50.79) * mm]});
            skFitSpline(sketch, "E185", {"points": [v(-15.66, 50.79) * mm, v(-15.46, 50.74) * mm, v(-15.28, 50.69) * mm, v(-15.26, 50.68) * mm]});
            skFitSpline(sketch, "E186", {"points": [v(-15.26, 50.68) * mm, v(-15.24, 50.68) * mm, v(-15.18, 50.66) * mm, v(-15.13, 50.64) * mm]});
            skFitSpline(sketch, "E187", {"points": [v(-15.13, 50.64) * mm, v(-15.08, 50.62) * mm, v(-14.95, 50.57) * mm, v(-14.84, 50.53) * mm]});
            skFitSpline(sketch, "E188", {"points": [v(-14.84, 50.53) * mm, v(-14.32, 50.33) * mm, v(-13.4, 49.8) * mm, v(-13.1, 49.53) * mm]});
            skFitSpline(sketch, "E189", {"points": [v(-13.1, 49.53) * mm, v(-13.04, 49.48) * mm, v(-13, 49.45) * mm, v(-12.99, 49.46) * mm]});
            skFitSpline(sketch, "E190", {"points": [v(-12.99, 49.46) * mm, v(-12.98, 49.47) * mm, v(-12.89, 49.63) * mm, v(-12.79, 49.82) * mm]});
            skFitSpline(sketch, "E191", {"points": [v(-12.79, 49.82) * mm, v(-12.54, 50.28) * mm, v(-12.3, 50.62) * mm, v(-11.9, 51.05) * mm]});
            skFitSpline(sketch, "E192", {"points": [v(-11.9, 51.05) * mm, v(-11.3, 51.7) * mm, v(-10.44, 52.35) * mm, v(-9.8, 52.67) * mm]});
            skFitSpline(sketch, "E193", {"points": [v(-9.8, 52.67) * mm, v(-8.65, 53.25) * mm, v(-7.15, 53.42) * mm, v(-5.85, 53.13) * mm]});
            skFitSpline(sketch, "E194", {"points": [v(-5.85, 53.13) * mm, v(-5.68, 53.09) * mm, v(-5.53, 53.06) * mm, v(-5.5, 53.05) * mm]});
            skFitSpline(sketch, "E195", {"points": [v(-5.5, 53.05) * mm, v(-5.48, 53.04) * mm, v(-5.41, 53.02) * mm, v(-5.37, 53) * mm]});
            skFitSpline(sketch, "E196", {"points": [v(-5.37, 53) * mm, v(-5.32, 52.99) * mm, v(-5.08, 52.9) * mm, v(-4.84, 52.8) * mm]});
            skFitSpline(sketch, "E197", {"points": [v(-4.84, 52.8) * mm, v(-4.35, 52.6) * mm, v(-3.38, 52.05) * mm, v(-2.88, 51.68) * mm]});
            skFitSpline(sketch, "E198", {"points": [v(-2.88, 51.68) * mm, v(-2.53, 51.41) * mm, v(-1.94, 50.85) * mm, v(-1.78, 50.63) * mm]});
            skFitSpline(sketch, "E199", {"points": [v(-1.46, 50.6) * mm, v(-1, 50.8) * mm, v(-0.07, 51.1) * mm, v(0.3, 51.16) * mm]});
            skFitSpline(sketch, "E200", {"points": [v(0.3, 51.16) * mm, v(1.11, 51.3) * mm, v(2.04, 51.07) * mm, v(2.84, 50.53) * mm]});
            skFitSpline(sketch, "E201", {"points": [v(3.3, 50.49) * mm, v(3.6, 50.66) * mm, v(3.95, 50.8) * mm, v(4.34, 50.92) * mm]});
            skFitSpline(sketch, "E202", {"points": [v(4.34, 50.92) * mm, v(4.77, 51.04) * mm, v(4.8, 51.05) * mm, v(5.43, 51.07) * mm]});
            skFitSpline(sketch, "E203", {"points": [v(5.43, 51.07) * mm, v(5.99, 51.1) * mm, v(6.67, 51.03) * mm, v(7, 50.9) * mm]});
            skFitSpline(sketch, "E204", {"points": [v(7, 50.9) * mm, v(7.03, 50.9) * mm, v(7.16, 50.85) * mm, v(7.28, 50.81) * mm]});
            skFitSpline(sketch, "E205", {"points": [v(7.28, 50.81) * mm, v(7.56, 50.71) * mm, v(8.07, 50.44) * mm, v(8.3, 50.26) * mm]});
            skFitSpline(sketch, "E206", {"points": [v(8.96, 50.34) * mm, v(9.92, 50.81) * mm, v(10.82, 50.96) * mm, v(11.82, 50.81) * mm]});
            skFitSpline(sketch, "E207", {"points": [v(11.82, 50.81) * mm, v(12.93, 50.64) * mm, v(14.03, 50.04) * mm, v(14.7, 49.22) * mm]});
            skFitSpline(sketch, "E208", {"points": [v(15.19, 49.27) * mm, v(17.3, 51.2) * mm, v(20.76, 51.4) * mm, v(22.98, 49.72) * mm]});
            skFitSpline(sketch, "E209", {"points": [v(22.98, 49.72) * mm, v(23.12, 49.61) * mm, v(23.37, 49.4) * mm, v(23.53, 49.23) * mm]});
            skFitSpline(sketch, "E210", {"points": [v(23.94, 49) * mm, v(24.38, 49.3) * mm, v(24.88, 49.44) * mm, v(25.66, 49.5) * mm]});
            skFitSpline(sketch, "E211", {"points": [v(25.66, 49.5) * mm, v(26.66, 49.6) * mm, v(27.47, 49.45) * mm, v(28.19, 49.04) * mm]});
            skFitSpline(sketch, "E212", {"points": [v(28.8, 48.98) * mm, v(29.54, 49.3) * mm, v(30.54, 49.41) * mm, v(31.26, 49.26) * mm]});
            skFitSpline(sketch, "E213", {"points": [v(31.26, 49.26) * mm, v(32.07, 49.1) * mm, v(32.7, 48.75) * mm, v(33.24, 48.17) * mm]});
            skFitSpline(sketch, "E214", {"points": [v(33.24, 48.17) * mm, v(33.8, 47.58) * mm, v(34.17, 46.76) * mm, v(34.27, 45.95) * mm]});
            skFitSpline(sketch, "E215", {"points": [v(34.27, 45.95) * mm, v(34.3, 45.74) * mm, v(34.32, 45.56) * mm, v(34.33, 45.55) * mm]});
            skFitSpline(sketch, "E216", {"points": [v(34.33, 45.55) * mm, v(34.34, 45.54) * mm, v(34.53, 45.52) * mm, v(34.77, 45.5) * mm]});
            skFitSpline(sketch, "E217", {"points": [v(34.77, 45.5) * mm, v(36.02, 45.37) * mm, v(37.2, 44.96) * mm, v(38.07, 44.36) * mm]});
            skFitSpline(sketch, "E218", {"points": [v(38.07, 44.36) * mm, v(38.33, 44.18) * mm, v(38.43, 44.14) * mm, v(38.46, 44.18) * mm]});
            skFitSpline(sketch, "E219", {"points": [v(38.46, 44.18) * mm, v(38.53, 44.26) * mm, v(38.87, 44.49) * mm, v(39.11, 44.61) * mm]});
            skFitSpline(sketch, "E220", {"points": [v(39.11, 44.61) * mm, v(39.46, 44.79) * mm, v(39.8, 44.86) * mm, v(40.25, 44.86) * mm]});
            skFitSpline(sketch, "E221", {"points": [v(40.25, 44.86) * mm, v(40.6, 44.86) * mm, v(40.73, 44.84) * mm, v(41.03, 44.74) * mm]});
            skFitSpline(sketch, "E222", {"points": [v(41.03, 44.74) * mm, v(41.92, 44.43) * mm, v(42.53, 43.73) * mm, v(42.72, 42.8) * mm]});
            skFitSpline(sketch, "E223", {"points": [v(42.72, 42.8) * mm, v(42.9, 41.85) * mm, v(42.52, 40.87) * mm, v(41.7, 40.23) * mm]});
            skFitSpline(sketch, "E224", {"points": [v(41.7, 40.23) * mm, v(41.4, 40) * mm, v(40.77, 39.78) * mm, v(40.37, 39.78) * mm]});
            skFitSpline(sketch, "E225", {"points": [v(39.94, 39.4) * mm, v(39.8, 39.13) * mm, v(39.68, 38.96) * mm, v(39.48, 38.75) * mm]});
            skFitSpline(sketch, "E226", {"points": [v(39.25, 38.2) * mm, v(39.28, 38.06) * mm, v(39.3, 37.7) * mm, v(39.3, 37.37) * mm]});
            skFitSpline(sketch, "E227", {"points": [v(39.3, 37.37) * mm, v(39.3, 36.89) * mm, v(39.29, 36.72) * mm, v(39.2, 36.37) * mm]});
            skFitSpline(sketch, "E228", {"points": [v(39.2, 36.37) * mm, v(38.98, 35.54) * mm, v(38.61, 34.9) * mm, v(37.97, 34.27) * mm]});
            skFitSpline(sketch, "E229", {"points": [v(37.97, 34.27) * mm, v(37.34, 33.66) * mm, v(36.64, 33.28) * mm, v(35.75, 33.09) * mm]});
            skFitSpline(sketch, "E230", {"points": [v(35.75, 33.09) * mm, v(35.37, 33) * mm, v(34.1, 32.97) * mm, v(33.78, 33.03) * mm]});
            skFitSpline(sketch, "E231", {"points": [v(33.78, 33.03) * mm, v(33.68, 33.05) * mm, v(33.39, 33.1) * mm, v(33.13, 33.16) * mm]});
            skFitSpline(sketch, "E232", {"points": [v(33.13, 33.16) * mm, v(32.52, 33.27) * mm, v(31.74, 33.53) * mm, v(31.17, 33.81) * mm]});
            skFitSpline(sketch, "E233", {"points": [v(31.17, 33.81) * mm, v(30.92, 33.93) * mm, v(30.7, 34.04) * mm, v(30.7, 34.06) * mm]});
            skFitSpline(sketch, "E234", {"points": [v(30.7, 34.06) * mm, v(30.68, 34.07) * mm, v(30.58, 34.15) * mm, v(30.46, 34.23) * mm]});
            skFitSpline(sketch, "E235", {"points": [v(30.46, 34.23) * mm, v(30.35, 34.3) * mm, v(30.11, 34.5) * mm, v(29.94, 34.67) * mm]});
            skFitSpline(sketch, "E236", {"points": [v(29.38, 34.84) * mm, v(29.04, 34.67) * mm, v(28.8, 34.6) * mm, v(28.4, 34.58) * mm]});
            skFitSpline(sketch, "E237", {"points": [v(28, 34.08) * mm, v(27.97, 33.82) * mm, v(27.93, 33.2) * mm, v(27.9, 32.68) * mm]});
            skFitSpline(sketch, "E238", {"points": [v(27.9, 32.68) * mm, v(27.83, 31.34) * mm, v(27.74, 30.02) * mm, v(27.64, 29.13) * mm]});
            skFitSpline(sketch, "E239", {"points": [v(27.64, 29.13) * mm, v(27.6, 28.7) * mm, v(27.55, 28.04) * mm, v(27.54, 27.65) * mm]});
            skFitSpline(sketch, "E240", {"points": [v(27.54, 27.65) * mm, v(27.5, 26.47) * mm, v(27.3, 25.12) * mm, v(27.05, 24.5) * mm]});
            skFitSpline(sketch, "E241", {"points": [v(27.05, 24.5) * mm, v(26.8, 23.86) * mm, v(26.37, 23.38) * mm, v(25.81, 23.12) * mm]});
            skFitSpline(sketch, "E242", {"points": [v(25.81, 23.12) * mm, v(25.31, 22.88) * mm, v(25.16, 22.86) * mm, v(23.94, 22.86) * mm]});
            skFitSpline(sketch, "E243", {"points": [v(23.94, 22.86) * mm, v(22.92, 22.86) * mm, v(22.82, 22.87) * mm, v(22.37, 22.97) * mm]});
            skFitSpline(sketch, "E244", {"points": [v(22.37, 22.97) * mm, v(21.8, 23.1) * mm, v(21.5, 23.22) * mm, v(21.17, 23.42) * mm]});
            skFitSpline(sketch, "E245", {"points": [v(20.59, 23.46) * mm, v(20.13, 23.3) * mm, v(19.73, 23.25) * mm, v(19.26, 23.28) * mm]});
            skFitSpline(sketch, "E246", {"points": [v(19.26, 23.28) * mm, v(18.13, 23.34) * mm, v(17.07, 23.87) * mm, v(16.15, 24.85) * mm]});
            skFitSpline(sketch, "E247", {"points": [v(16.15, 24.85) * mm, v(15.92, 25.1) * mm, v(15.46, 25.7) * mm, v(15.37, 25.87) * mm]});
            skFitSpline(sketch, "E248", {"points": [v(15.37, 25.87) * mm, v(15.36, 25.88) * mm, v(15.23, 25.84) * mm, v(15.06, 25.8) * mm]});
            skFitSpline(sketch, "E249", {"points": [v(15.06, 25.8) * mm, v(14.3, 25.58) * mm, v(12.12, 25.52) * mm, v(11.5, 25.69) * mm]});
            skFitSpline(sketch, "E250", {"points": [v(11.5, 25.69) * mm, v(11.01, 25.82) * mm, v(10.54, 26.09) * mm, v(10.19, 26.42) * mm]});
            skFitSpline(sketch, "E251", {"points": [v(9.7, 26.63) * mm, v(9.27, 26.32) * mm, v(8.56, 26.06) * mm, v(7.94, 25.97) * mm]});
            skFitSpline(sketch, "E252", {"points": [v(7.94, 25.97) * mm, v(7.37, 25.9) * mm, v(6.38, 26) * mm, v(5.75, 26.2) * mm]});
            skFitSpline(sketch, "E253", {"points": [v(5.75, 26.2) * mm, v(5.45, 26.3) * mm, v(4.95, 26.53) * mm, v(4.76, 26.66) * mm]});
            skFitSpline(sketch, "E254", {"points": [v(4.76, 26.66) * mm, v(4.7, 26.71) * mm, v(4.63, 26.75) * mm, v(4.61, 26.75) * mm]});
            skFitSpline(sketch, "E255", {"points": [v(4.61, 26.75) * mm, v(4.58, 26.75) * mm, v(4.57, 26.76) * mm, v(4.2, 27.1) * mm]});
            skFitSpline(sketch, "E256", {"points": [v(4.2, 27.1) * mm, v(3.96, 27.32) * mm, v(3.9, 27.35) * mm, v(3.8, 27.33) * mm]});
            skFitSpline(sketch, "E257", {"points": [v(3.8, 27.33) * mm, v(3.3, 27.23) * mm, v(2.9, 27.2) * mm, v(2.07, 27.2) * mm]});
            skFitSpline(sketch, "E258", {"points": [v(2.07, 27.2) * mm, v(1.01, 27.2) * mm, v(0.81, 27.23) * mm, v(0.27, 27.5) * mm]});
            skFitSpline(sketch, "E259", {"points": [v(-0.2, 27.55) * mm, v(-0.69, 27.26) * mm, v(-1.65, 27.06) * mm, v(-2.25, 27.11) * mm]});
            skFitSpline(sketch, "E260", {"points": [v(-2.25, 27.11) * mm, v(-2.55, 27.14) * mm, v(-3, 27.22) * mm, v(-3.16, 27.28) * mm]});
            skFitSpline(sketch, "E261", {"points": [v(-3.16, 27.28) * mm, v(-3.2, 27.3) * mm, v(-3.27, 27.23) * mm, v(-3.4, 27) * mm]});
            skFitSpline(sketch, "E262", {"points": [v(-3.4, 27) * mm, v(-3.63, 26.63) * mm, v(-4.07, 26.16) * mm, v(-4.42, 25.9) * mm]});
            skFitSpline(sketch, "E263", {"points": [v(-4.42, 25.9) * mm, v(-4.81, 25.63) * mm, v(-5.7, 25.22) * mm, v(-6.12, 25.11) * mm]});
            skFitSpline(sketch, "E264", {"points": [v(-6.12, 25.11) * mm, v(-6.56, 25.01) * mm, v(-6.97, 25) * mm, v(-7.73, 25.1) * mm]});
            skFitSpline(sketch, "E265", {"points": [v(-7.73, 25.1) * mm, v(-8.5, 25.18) * mm, v(-8.85, 25.26) * mm, v(-9.21, 25.44) * mm]});
            skFitSpline(sketch, "E266", {"points": [v(-9.21, 25.44) * mm, v(-9.62, 25.63) * mm, v(-9.87, 25.8) * mm, v(-10.21, 26.14) * mm]});
            skFitSpline(sketch, "E267", {"points": [v(-10.7, 26.2) * mm, v(-10.8, 26.08) * mm, v(-11.03, 25.87) * mm, v(-11.2, 25.73) * mm]});
            skFitSpline(sketch, "E268", {"points": [v(-11.2, 25.73) * mm, v(-11.38, 25.6) * mm, v(-11.52, 25.46) * mm, v(-11.53, 25.45) * mm]});
            skFitSpline(sketch, "E269", {"points": [v(-11.53, 25.45) * mm, v(-11.54, 25.43) * mm, v(-11.57, 25.41) * mm, v(-11.6, 25.41) * mm]});
            skFitSpline(sketch, "E270", {"points": [v(-11.6, 25.41) * mm, v(-11.64, 25.41) * mm, v(-11.67, 25.4) * mm, v(-11.67, 25.37) * mm]});
            skFitSpline(sketch, "E271", {"points": [v(-11.67, 25.37) * mm, v(-11.67, 25.35) * mm, v(-11.69, 25.33) * mm, v(-11.7, 25.33) * mm]});
            skFitSpline(sketch, "E272", {"points": [v(-11.7, 25.33) * mm, v(-11.73, 25.33) * mm, v(-11.9, 25.25) * mm, v(-12.08, 25.15) * mm]});
            skFitSpline(sketch, "E273", {"points": [v(-12.08, 25.15) * mm, v(-12.27, 25.05) * mm, v(-12.44, 24.96) * mm, v(-12.46, 24.96) * mm]});
            skFitSpline(sketch, "E274", {"points": [v(-12.46, 24.96) * mm, v(-12.49, 24.95) * mm, v(-12.62, 24.9) * mm, v(-12.76, 24.86) * mm]});
            skFitSpline(sketch, "E275", {"points": [v(-12.76, 24.86) * mm, v(-13.43, 24.62) * mm, v(-14.86, 24.5) * mm, v(-15.79, 24.6) * mm]});
            skFitSpline(sketch, "E276", {"points": [v(-15.79, 24.6) * mm, v(-16.05, 24.62) * mm, v(-16.3, 24.65) * mm, v(-16.33, 24.67) * mm]});
            skFitSpline(sketch, "E277", {"points": [v(-16.33, 24.67) * mm, v(-16.37, 24.68) * mm, v(-16.4, 24.6) * mm, v(-16.41, 24.24) * mm]});
            skFitSpline(sketch, "E278", {"points": [v(-16.41, 24.24) * mm, v(-16.47, 23.24) * mm, v(-16.9, 22.57) * mm, v(-18.03, 21.7) * mm]});
            skFitSpline(sketch, "E279", {"points": [v(-18.03, 21.7) * mm, v(-18.19, 21.58) * mm, v(-18.73, 21.33) * mm, v(-19.07, 21.2) * mm]});
            skFitSpline(sketch, "E280", {"points": [v(-19.07, 21.2) * mm, v(-19.83, 20.94) * mm, v(-20.74, 20.78) * mm, v(-22.23, 20.64) * mm]});
            skFitSpline(sketch, "E281", {"points": [v(-22.23, 20.64) * mm, v(-22.75, 20.59) * mm, v(-23.35, 20.53) * mm, v(-23.56, 20.5) * mm]});
            skFitSpline(sketch, "E282", {"points": [v(-23.56, 20.5) * mm, v(-24, 20.47) * mm, v(-24.04, 20.47) * mm, v(-24.47, 20.52) * mm]});
            skSolve(sketch);
        }
        {
            var Q0;
            Q0=qSketchRegion(id+"F11",true);
            extrude(context, id + "F12", {"entities" : qUnion([Q0]), "operationType" : NewBodyOperationType.REMOVE, "oppositeDirection" : true, "depth" : 30 * mm, "offsetDistance" : 25 * mm});
        }
        {
            var Q0;
            Q0=qCreatedBy(makeId("Front.planeOp"),FACE);
            var sketch = newSketch(context, id + "F13", { "sketchPlane" : qUnion([Q0])});
            skLineSegment(sketch, "E283.bottom", {"start": v(66.54, 56.4) * mm, "end": v(62.54, 56.4) * mm});
            skLineSegment(sketch, "E283.top", {"start": v(66.54, 18.4) * mm, "end": v(62.54, 18.4) * mm});
            skLineSegment(sketch, "E283.left", {"start": v(66.54, 56.4) * mm, "end": v(66.54, 18.4) * mm});
            skLineSegment(sketch, "E283.right", {"start": v(62.54, 56.4) * mm, "end": v(62.54, 18.4) * mm});
            skSolve(sketch);
        }
        {
            var Q0;
            Q0=qSketchRegion(id+"F13",true);
            var Q1;
            Q1=sQuery(id+"F0.wireOp",EDGE,"E4");
            revolve(context, id + "F14", {"operationType" : NewBodyOperationType.ADD, "entities" : qUnion([Q0]), "axis" : qUnion([Q1]), "revolveType" : RevolveType.ONE_DIRECTION, "oppositeDirection" : true, "angle" : 180 * degree});
        }
    });
